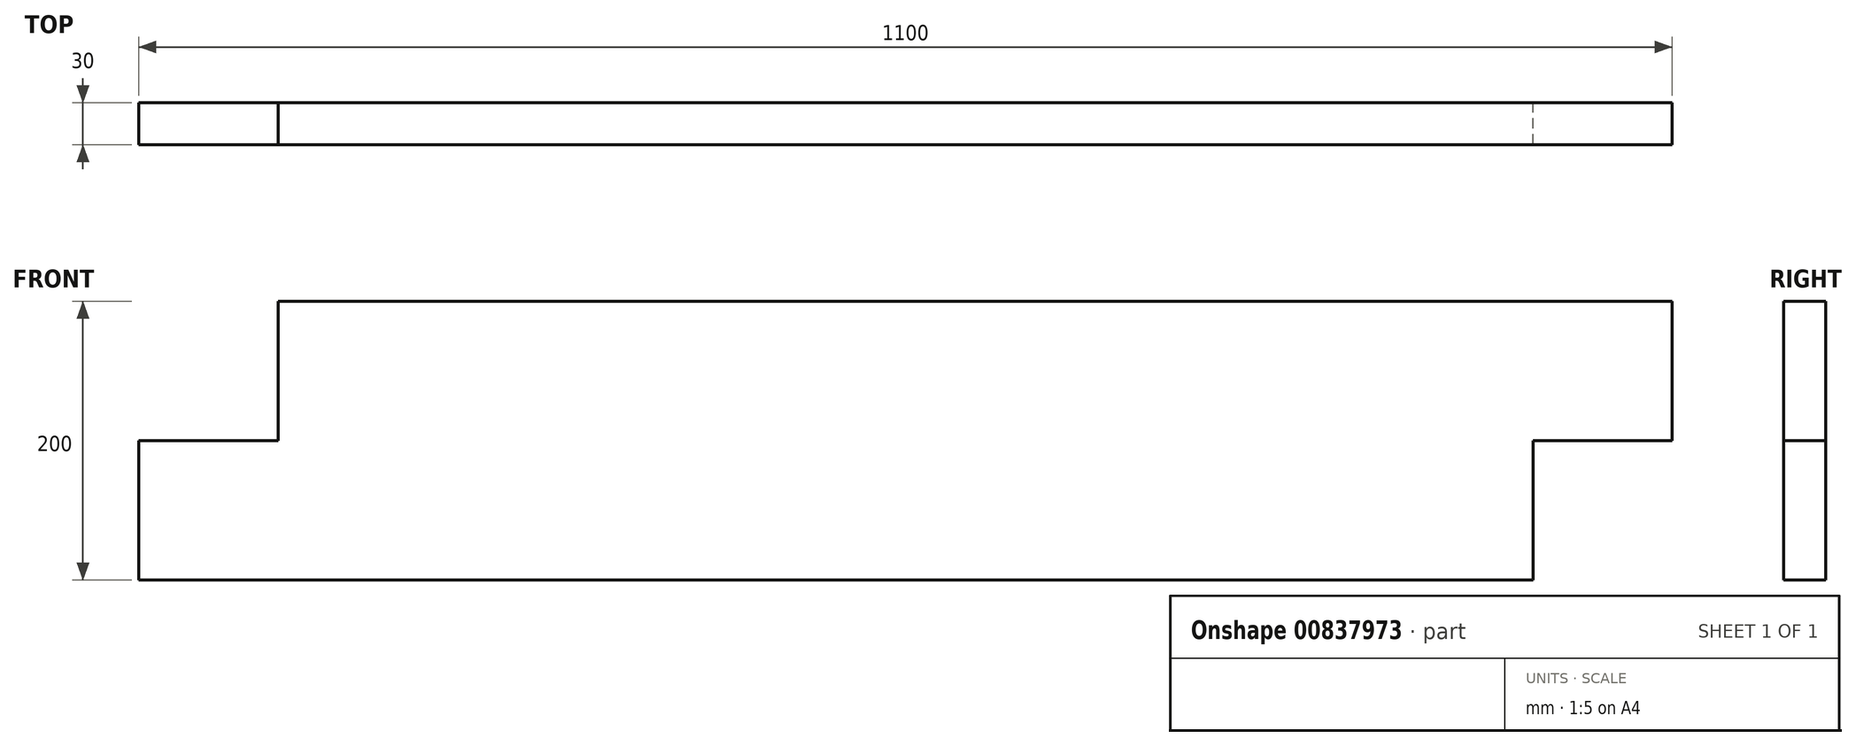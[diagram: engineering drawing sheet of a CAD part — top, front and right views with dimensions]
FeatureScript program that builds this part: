
annotation { "Feature Type Name" : "Feature", "Feature Type Description" : "" }
export const myFeature = defineFeature(function(context is Context, id is Id, definition is map)
    precondition{}
    {
        {
            var Q0;
            Q0=qCreatedBy(makeId("Front.planeOp"),FACE);
            var sketch = newSketch(context, id + "F0", { "sketchPlane" : qUnion([Q0])});
            skLineSegment(sketch, "E0", {"start": v(-499.03, -100) * mm, "end": v(-499.03, 0) * mm});
            skLineSegment(sketch, "E1", {"start": v(-499.03, 0) * mm, "end": v(-399.03, 0) * mm});
            skLineSegment(sketch, "E2", {"start": v(-399.03, 0) * mm, "end": v(-399.03, 100) * mm});
            skLineSegment(sketch, "E3", {"start": v(-399.03, 100) * mm, "end": v(600.97, 100) * mm});
            skLineSegment(sketch, "E4", {"start": v(600.97, 100) * mm, "end": v(600.97, 0) * mm});
            skLineSegment(sketch, "E5", {"start": v(600.97, 0) * mm, "end": v(500.97, 0) * mm});
            skLineSegment(sketch, "E6", {"start": v(500.97, 0) * mm, "end": v(500.97, -100) * mm});
            skLineSegment(sketch, "E7", {"start": v(500.97, -100) * mm, "end": v(-499.03, -100) * mm});
            skSolve(sketch);
        }
        {
            var Q0;
            Q0=makeQuery(id+"F0.imprint","IMPRINT",FACE,{"disambiguationData":[TD([[makeQuery(id+"F0.imprint","IMPRINT",EDGE,{"derivedFrom":sQuery(id+"F0.wireOp",EDGE,"E0")}),-1.0]])]});
            extrude(context, id + "F1", {"entities" : qUnion([Q0]), "depth" : 30 * mm, "offsetDistance" : 25 * mm});
        }
    });
